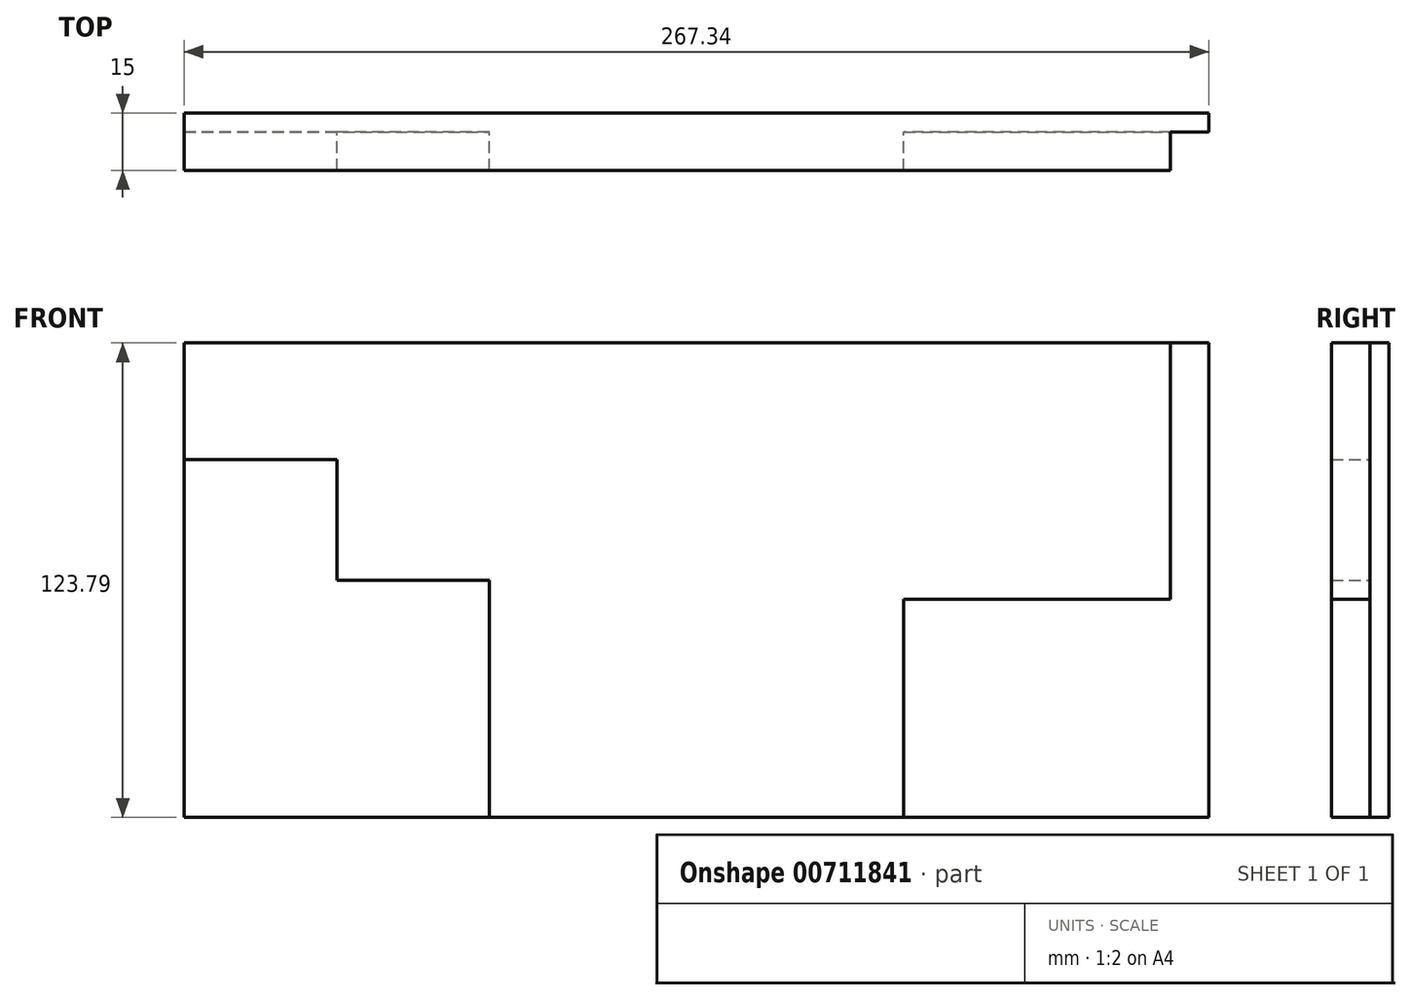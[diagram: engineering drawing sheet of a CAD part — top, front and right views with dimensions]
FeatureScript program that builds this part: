
annotation { "Feature Type Name" : "Feature", "Feature Type Description" : "" }
export const myFeature = defineFeature(function(context is Context, id is Id, definition is map)
    precondition{}
    {
        {
            var Q0;
            Q0=qCreatedBy(makeId("Front.planeOp"),FACE);
            var sketch = newSketch(context, id + "F0", { "sketchPlane" : qUnion([Q0])});
            skLineSegment(sketch, "E0.bottom", {"start": v(-130.9, 59.85) * mm, "end": v(126.45, 59.85) * mm});
            skLineSegment(sketch, "E0.top", {"start": v(-130.9, -63.94) * mm, "end": v(126.45, -63.94) * mm});
            skLineSegment(sketch, "E0.left", {"start": v(-130.9, 59.85) * mm, "end": v(-130.9, -63.94) * mm});
            skLineSegment(sketch, "E0.right", {"start": v(126.45, 59.85) * mm, "end": v(126.45, -63.94) * mm});
            skLineSegment(sketch, "E1.bottom", {"start": v(126.45, -7.07) * mm, "end": v(56.83, -7.07) * mm});
            skLineSegment(sketch, "E1.top", {"start": v(126.45, -63.94) * mm, "end": v(56.83, -63.94) * mm});
            skLineSegment(sketch, "E1.left", {"start": v(126.45, -7.07) * mm, "end": v(126.45, -63.94) * mm});
            skLineSegment(sketch, "E1.right", {"start": v(56.83, -7.07) * mm, "end": v(56.83, -63.94) * mm});
            skLineSegment(sketch, "E2.bottom", {"start": v(-51.24, -63.94) * mm, "end": v(-130.9, -63.94) * mm});
            skLineSegment(sketch, "E2.top", {"start": v(-51.24, -2.04) * mm, "end": v(-130.9, -2.04) * mm});
            skLineSegment(sketch, "E2.left", {"start": v(-51.24, -63.94) * mm, "end": v(-51.24, -2.04) * mm});
            skLineSegment(sketch, "E2.right", {"start": v(-130.9, -63.94) * mm, "end": v(-130.9, -2.04) * mm});
            skLineSegment(sketch, "E3.bottom", {"start": v(-91.06, -2.04) * mm, "end": v(-130.9, -2.04) * mm});
            skLineSegment(sketch, "E3.top", {"start": v(-91.06, 29.4) * mm, "end": v(-130.9, 29.4) * mm});
            skLineSegment(sketch, "E3.left", {"start": v(-91.06, -2.04) * mm, "end": v(-91.06, 29.4) * mm});
            skLineSegment(sketch, "E3.right", {"start": v(-130.9, -2.04) * mm, "end": v(-130.9, 29.4) * mm});
            skSolve(sketch);
        }
        {
            var Q0;
            Q0=makeQuery(id+"F0.imprint","IMPRINT",FACE,{"disambiguationData":[TD([[makeQuery(id+"F0.imprint","IMPRINT",EDGE,{"derivedFrom":sQuery(id+"F0.wireOp",EDGE,"E0.bottom")}),-1.0]])]});
            extrude(context, id + "F1", {"entities" : qUnion([Q0]), "depth" : 10 * mm, "offsetDistance" : 25 * mm});
        }
        {
            var Q0;
            Q0=makeQuery(id+"F1.opExtrude","CAP_FACE",FACE,{"disambiguationData":[OSD([sQuery(id+"F0.wireOp",EDGE,"E0.bottom"),sQuery(id+"F0.wireOp",EDGE,"E0.top"),sQuery(id+"F0.wireOp",EDGE,"E0.left"),sQuery(id+"F0.wireOp",EDGE,"E0.right"),sQuery(id+"F0.wireOp",EDGE,"E1.bottom"),sQuery(id+"F0.wireOp",EDGE,"E1.right"),sQuery(id+"F0.wireOp",EDGE,"E2.top"),sQuery(id+"F0.wireOp",EDGE,"E2.left"),sQuery(id+"F0.wireOp",EDGE,"E3.top"),sQuery(id+"F0.wireOp",EDGE,"E3.left")])],"isStart":true});
            var sketch = newSketch(context, id + "F2", { "sketchPlane" : qUnion([Q0])});
            skLineSegment(sketch, "E4.bottom", {"start": v(130.9, -63.94) * mm, "end": v(-126.45, -63.94) * mm});
            skLineSegment(sketch, "E4.top", {"start": v(130.9, 59.85) * mm, "end": v(-126.45, 59.85) * mm});
            skLineSegment(sketch, "E4.left", {"start": v(130.9, -63.94) * mm, "end": v(130.9, 59.85) * mm});
            skLineSegment(sketch, "E4.right", {"start": v(-126.45, -63.94) * mm, "end": v(-126.45, 59.85) * mm});
            skSolve(sketch);
        }
        {
            var Q0;
            Q0=makeQuery(id+"F2.imprint","IMPRINT",FACE,{"disambiguationData":[TD([[makeQuery(id+"F2.imprint","IMPRINT",EDGE,{"derivedFrom":makeQuery(id+"F1.opExtrude","CAP_EDGE",EDGE,{"disambiguationData":[OSD([sQuery(id+"F0.wireOp",EDGE,"E2.top")])],"isStart":true})}),-1.0]])]});
            var Q1;
            {var subQ4=makeQuery(id+"F1.opExtrude","CAP_EDGE",EDGE,{"disambiguationData":[OSD([sQuery(id+"F0.wireOp",EDGE,"E1.bottom")])],"isStart":true});Q1=makeQuery(id+"F2.imprint","IMPRINT",FACE,{"disambiguationData":[TD([[makeQuery(id+"F2.imprint","IMPRINT",EDGE,{"derivedFrom":subQ4}),-1.0]])]});}
            var Q2;
            {var subQ1=sQuery(id+"F2.wireOp",EDGE,"E4.top");Q2=makeQuery(id+"F2.imprint","IMPRINT",FACE,{"disambiguationData":[TD([[makeQuery(id+"F2.imprint","IMPRINT",EDGE,{"derivedFrom":subQ1}),1.0]])]});}
            extrude(context, id + "F3", {"entities" : qUnion([Q0, Q1, Q2]), "operationType" : NewBodyOperationType.ADD, "depth" : 5 * mm, "offsetDistance" : 25 * mm});
        }
        {
            var Q0;
            Q0=makeQuery(id+"F3.boolean.opBoolean","MERGE",FACE,{"derivedFrom":[makeQuery(id+"F1.opExtrude","SWEPT_FACE",FACE,{"disambiguationData":[OSD([sQuery(id+"F0.wireOp",EDGE,"E0.right")])]}),makeQuery(id+"F3.opExtrude","SWEPT_FACE",FACE,{"disambiguationData":[OSD([sQuery(id+"F2.wireOp",EDGE,"E4.right")])]})]});
            var sketch = newSketch(context, id + "F4", { "sketchPlane" : qUnion([Q0])});
            skLineSegment(sketch, "E5.bottom", {"start": v(5, 59.85) * mm, "end": v(0, 59.85) * mm});
            skLineSegment(sketch, "E5.top", {"start": v(5, -63.94) * mm, "end": v(0, -63.94) * mm});
            skLineSegment(sketch, "E5.left", {"start": v(5, 59.85) * mm, "end": v(5, -63.94) * mm});
            skLineSegment(sketch, "E5.right", {"start": v(0, 59.85) * mm, "end": v(0, -63.94) * mm});
            skSolve(sketch);
        }
        {
            var Q0;
            Q0 = qSketchRegion(id + "F4", true);
            extrude(context, id + "F5", {"entities" : qUnion([Q0]), "operationType" : NewBodyOperationType.ADD, "depth" : 10 * mm, "offsetDistance" : 25 * mm});
        }
    });
